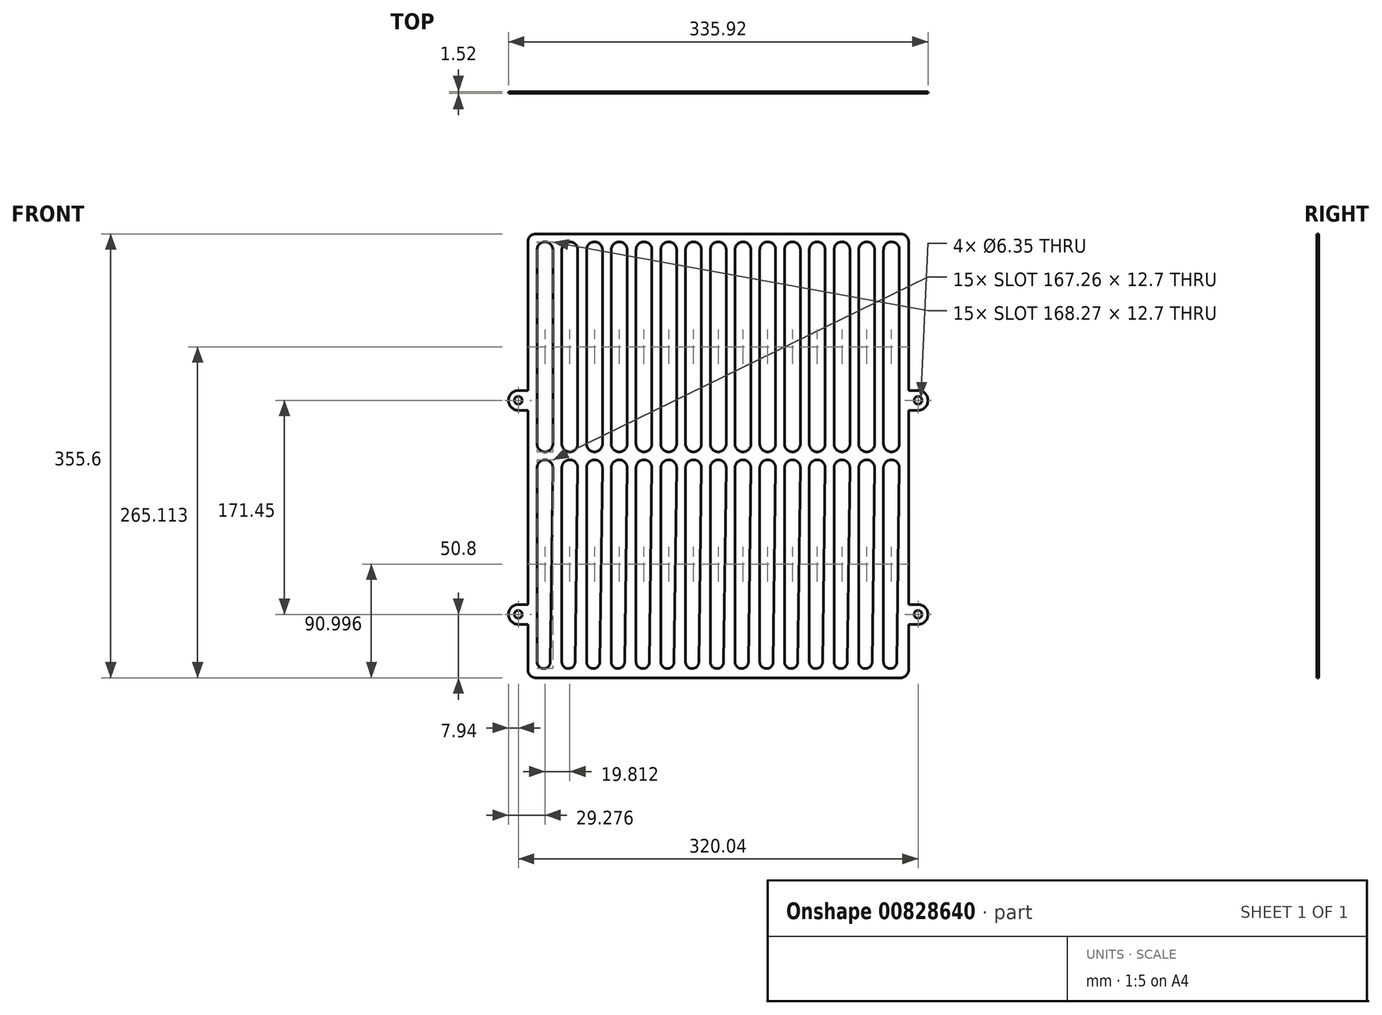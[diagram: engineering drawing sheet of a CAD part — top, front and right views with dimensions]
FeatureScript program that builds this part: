
annotation { "Feature Type Name" : "Feature", "Feature Type Description" : "" }
export const myFeature = defineFeature(function(context is Context, id is Id, definition is map)
    precondition{}
    {
        {
            var Q0;
            Q0=qCreatedBy(makeId("Front.planeOp"),FACE);
            var sketch = newSketch(context, id + "F0", { "sketchPlane" : qUnion([Q0])});
            skLineSegment(sketch, "E0.bottom", {"start": v(-323.85, -177.8) * mm, "end": v(-31.75, -177.8) * mm});
            skLineSegment(sketch, "E0.top", {"start": v(-323.85, 177.8) * mm, "end": v(-31.75, 177.8) * mm});
            skLineSegment(sketch, "E0.left", {"start": v(-330.2, -171.45) * mm, "end": v(-330.2, -134.94) * mm});
            skLineSegment(sketch, "E0.right", {"start": v(-25.4, -171.45) * mm, "end": v(-25.4, -134.94) * mm});
            skPoint(sketch, "E0.middle", {"position": v(-177.8, 0) * mm});
            skArc(sketch, "E1", {"start": v(-337.82, -119.06) * mm, "mid": v(-345.76, -127) * mm, "end": v(-337.82, -134.94) * mm});
            skArc(sketch, "E2", {"start": v(-17.78, -134.94) * mm, "mid": v(-9.84, -127) * mm, "end": v(-17.78, -119.06) * mm});
            skCircle(sketch, "E3", {"center": v(-17.78, -127) * mm, "radius": 3.18 * mm});
            skCircle(sketch, "E4", {"center": v(-337.82, -127) * mm, "radius": 3.18 * mm});
            skLineSegment(sketch, "E5", {"start": v(-17.78, -134.94) * mm, "end": v(-25.4, -134.94) * mm});
            skLineSegment(sketch, "E6", {"start": v(-25.4, -134.94) * mm, "end": v(-25.4, -134.94) * mm});
            skLineSegment(sketch, "E7", {"start": v(-17.78, -119.06) * mm, "end": v(-25.4, -119.06) * mm});
            skLineSegment(sketch, "E8", {"start": v(-337.82, -134.94) * mm, "end": v(-330.2, -134.94) * mm});
            skLineSegment(sketch, "E9", {"start": v(-330.2, -134.94) * mm, "end": v(-330.2, -134.94) * mm});
            skLineSegment(sketch, "E10", {"start": v(-337.82, -119.06) * mm, "end": v(-330.2, -119.06) * mm});
            skLineSegment(sketch, "E11.trimOffspring", {"start": v(-330.2, -119.06) * mm, "end": v(-330.2, 36.51) * mm});
            skLineSegment(sketch, "E12.trimOffspring", {"start": v(-25.4, -119.06) * mm, "end": v(-25.4, 36.51) * mm});
            skPoint(sketch, "E13.end.orphan", {"position": v(-25.4, 29.37) * mm});
            skPoint(sketch, "E13.start.orphan", {"position": v(-330.2, 29.37) * mm});
            skLineSegment(sketch, "E14.MirrorCS", {"start": v(-337.82, 52.39) * mm, "end": v(-330.2, 52.39) * mm});
            skArc(sketch, "E15.MirrorCS", {"start": v(-337.82, 36.51) * mm, "mid": v(-345.76, 44.45) * mm, "end": v(-337.82, 52.39) * mm});
            skCircle(sketch, "E16.MirrorC", {"center": v(-337.82, 44.45) * mm, "radius": 3.18 * mm});
            skLineSegment(sketch, "E17.MirrorCS", {"start": v(-337.82, 36.51) * mm, "end": v(-330.2, 36.51) * mm});
            skLineSegment(sketch, "E18.MirrorCS", {"start": v(-17.78, 52.39) * mm, "end": v(-25.4, 52.39) * mm});
            skArc(sketch, "E19.MirrorCS", {"start": v(-17.78, 52.39) * mm, "mid": v(-9.84, 44.45) * mm, "end": v(-17.78, 36.51) * mm});
            skCircle(sketch, "E20.MirrorC", {"center": v(-17.78, 44.45) * mm, "radius": 3.18 * mm});
            skLineSegment(sketch, "E21.MirrorCS", {"start": v(-17.78, 36.51) * mm, "end": v(-25.4, 36.51) * mm});
            skLineSegment(sketch, "E22.trimOffspring", {"start": v(-25.4, 52.39) * mm, "end": v(-25.4, 171.45) * mm});
            skPoint(sketch, "E23.start.orphan", {"position": v(-330.2, -41.28) * mm});
            skLineSegment(sketch, "E24.trimOffspring", {"start": v(-330.2, 52.39) * mm, "end": v(-330.2, 171.45) * mm});
            skArc(sketch, "E25.0.startCap", {"start": v(-322.83, 165.1) * mm, "mid": v(-316.48, 171.45) * mm, "end": v(-310.13, 165.1) * mm});
            skArc(sketch, "E25.0.endCap", {"start": v(-310.13, 9.52) * mm, "mid": v(-316.48, 3.17) * mm, "end": v(-322.83, 9.52) * mm});
            skLineSegment(sketch, "E25.0.left", {"start": v(-310.13, 165.1) * mm, "end": v(-310.13, 9.52) * mm});
            skLineSegment(sketch, "E25.0.right", {"start": v(-322.83, 165.1) * mm, "end": v(-322.83, 9.52) * mm});
            skArc(sketch, "E25.1.startCap", {"start": v(-322.83, -9.53) * mm, "mid": v(-316.44, -3.18) * mm, "end": v(-310.13, -9.6) * mm});
            skArc(sketch, "E25.1.endCap", {"start": v(-312.17, -165.17) * mm, "mid": v(-317.53, -170.43) * mm, "end": v(-322.83, -165.1) * mm});
            skLineSegment(sketch, "E25.1.left", {"start": v(-310.13, -9.6) * mm, "end": v(-312.17, -165.17) * mm});
            skLineSegment(sketch, "E25.1.right", {"start": v(-322.83, -9.53) * mm, "end": v(-322.83, -165.1) * mm});
            skLineSegment(sketch, "E26.1.0.0", {"start": v(-290.32, 165.1) * mm, "end": v(-290.32, 9.53) * mm});
            skArc(sketch, "E26.1.0.1", {"start": v(-290.32, 9.53) * mm, "mid": v(-296.67, 3.17) * mm, "end": v(-303.02, 9.52) * mm});
            skLineSegment(sketch, "E26.1.0.2", {"start": v(-303.02, 165.1) * mm, "end": v(-303.02, 9.52) * mm});
            skArc(sketch, "E26.1.0.3", {"start": v(-303.02, 165.1) * mm, "mid": v(-296.67, 171.45) * mm, "end": v(-290.32, 165.1) * mm});
            skLineSegment(sketch, "E26.2.0.0", {"start": v(-270.51, 165.1) * mm, "end": v(-270.51, 9.52) * mm});
            skArc(sketch, "E26.2.0.1", {"start": v(-270.51, 9.52) * mm, "mid": v(-276.86, 3.17) * mm, "end": v(-283.21, 9.52) * mm});
            skLineSegment(sketch, "E26.2.0.2", {"start": v(-283.21, 165.1) * mm, "end": v(-283.21, 9.52) * mm});
            skArc(sketch, "E26.2.0.3", {"start": v(-283.21, 165.1) * mm, "mid": v(-276.86, 171.45) * mm, "end": v(-270.51, 165.1) * mm});
            skLineSegment(sketch, "E26.3.0.0", {"start": v(-250.7, 165.1) * mm, "end": v(-250.7, 9.52) * mm});
            skArc(sketch, "E26.3.0.1", {"start": v(-250.7, 9.52) * mm, "mid": v(-257.05, 3.17) * mm, "end": v(-263.4, 9.52) * mm});
            skLineSegment(sketch, "E26.3.0.2", {"start": v(-263.4, 165.1) * mm, "end": v(-263.4, 9.52) * mm});
            skArc(sketch, "E26.3.0.3", {"start": v(-263.4, 165.1) * mm, "mid": v(-257.05, 171.45) * mm, "end": v(-250.7, 165.1) * mm});
            skLineSegment(sketch, "E26.4.0.0", {"start": v(-230.89, 165.1) * mm, "end": v(-230.89, 9.52) * mm});
            skArc(sketch, "E26.4.0.1", {"start": v(-230.89, 9.52) * mm, "mid": v(-237.24, 3.17) * mm, "end": v(-243.59, 9.52) * mm});
            skLineSegment(sketch, "E26.4.0.2", {"start": v(-243.59, 165.1) * mm, "end": v(-243.59, 9.52) * mm});
            skArc(sketch, "E26.4.0.3", {"start": v(-243.59, 165.1) * mm, "mid": v(-237.24, 171.45) * mm, "end": v(-230.89, 165.1) * mm});
            skLineSegment(sketch, "E26.5.0.0", {"start": v(-211.07, 165.1) * mm, "end": v(-211.07, 9.52) * mm});
            skArc(sketch, "E26.5.0.1", {"start": v(-211.07, 9.52) * mm, "mid": v(-217.42, 3.17) * mm, "end": v(-223.77, 9.52) * mm});
            skLineSegment(sketch, "E26.5.0.2", {"start": v(-223.77, 165.1) * mm, "end": v(-223.77, 9.52) * mm});
            skArc(sketch, "E26.5.0.3", {"start": v(-223.77, 165.1) * mm, "mid": v(-217.42, 171.45) * mm, "end": v(-211.07, 165.1) * mm});
            skLineSegment(sketch, "E26.6.0.0", {"start": v(-191.26, 165.1) * mm, "end": v(-191.26, 9.52) * mm});
            skArc(sketch, "E26.6.0.1", {"start": v(-191.26, 9.52) * mm, "mid": v(-197.61, 3.17) * mm, "end": v(-203.96, 9.52) * mm});
            skLineSegment(sketch, "E26.6.0.2", {"start": v(-203.96, 165.1) * mm, "end": v(-203.96, 9.52) * mm});
            skArc(sketch, "E26.6.0.3", {"start": v(-203.96, 165.1) * mm, "mid": v(-197.61, 171.45) * mm, "end": v(-191.26, 165.1) * mm});
            skLineSegment(sketch, "E26.7.0.0", {"start": v(-171.45, 165.1) * mm, "end": v(-171.45, 9.52) * mm});
            skArc(sketch, "E26.7.0.1", {"start": v(-171.45, 9.52) * mm, "mid": v(-177.8, 3.17) * mm, "end": v(-184.15, 9.52) * mm});
            skLineSegment(sketch, "E26.7.0.2", {"start": v(-184.15, 165.1) * mm, "end": v(-184.15, 9.52) * mm});
            skArc(sketch, "E26.7.0.3", {"start": v(-184.15, 165.1) * mm, "mid": v(-177.8, 171.45) * mm, "end": v(-171.45, 165.1) * mm});
            skLineSegment(sketch, "E26.8.0.0", {"start": v(-151.64, 165.1) * mm, "end": v(-151.64, 9.52) * mm});
            skArc(sketch, "E26.8.0.1", {"start": v(-151.64, 9.52) * mm, "mid": v(-157.99, 3.17) * mm, "end": v(-164.34, 9.52) * mm});
            skLineSegment(sketch, "E26.8.0.2", {"start": v(-164.34, 165.1) * mm, "end": v(-164.34, 9.52) * mm});
            skArc(sketch, "E26.8.0.3", {"start": v(-164.34, 165.1) * mm, "mid": v(-157.99, 171.45) * mm, "end": v(-151.64, 165.1) * mm});
            skLineSegment(sketch, "E26.9.0.0", {"start": v(-131.83, 165.1) * mm, "end": v(-131.83, 9.52) * mm});
            skArc(sketch, "E26.9.0.1", {"start": v(-131.83, 9.52) * mm, "mid": v(-138.18, 3.17) * mm, "end": v(-144.53, 9.52) * mm});
            skLineSegment(sketch, "E26.9.0.2", {"start": v(-144.53, 165.1) * mm, "end": v(-144.53, 9.52) * mm});
            skArc(sketch, "E26.9.0.3", {"start": v(-144.53, 165.1) * mm, "mid": v(-138.18, 171.45) * mm, "end": v(-131.83, 165.1) * mm});
            skLineSegment(sketch, "E26.10.0.0", {"start": v(-112.01, 165.1) * mm, "end": v(-112.01, 9.52) * mm});
            skArc(sketch, "E26.10.0.1", {"start": v(-112.01, 9.52) * mm, "mid": v(-118.36, 3.17) * mm, "end": v(-124.71, 9.52) * mm});
            skLineSegment(sketch, "E26.10.0.2", {"start": v(-124.71, 165.1) * mm, "end": v(-124.71, 9.52) * mm});
            skArc(sketch, "E26.10.0.3", {"start": v(-124.71, 165.1) * mm, "mid": v(-118.36, 171.45) * mm, "end": v(-112.01, 165.1) * mm});
            skLineSegment(sketch, "E26.11.0.0", {"start": v(-92.2, 165.1) * mm, "end": v(-92.2, 9.52) * mm});
            skArc(sketch, "E26.11.0.1", {"start": v(-92.2, 9.52) * mm, "mid": v(-98.55, 3.17) * mm, "end": v(-104.9, 9.52) * mm});
            skLineSegment(sketch, "E26.11.0.2", {"start": v(-104.9, 165.1) * mm, "end": v(-104.9, 9.52) * mm});
            skArc(sketch, "E26.11.0.3", {"start": v(-104.9, 165.1) * mm, "mid": v(-98.55, 171.45) * mm, "end": v(-92.2, 165.1) * mm});
            skLineSegment(sketch, "E26.direction1", {"start": v(-310.13, 9.52) * mm, "end": v(-290.32, 9.52) * mm, "construction": true});
            skLineSegment(sketch, "E26.direction2", {"start": v(-310.13, 9.52) * mm, "end": v(-310.13, 34.92) * mm, "construction": true});
            skLineSegment(sketch, "E27.0.12.0", {"start": v(-72.4, 165.1) * mm, "end": v(-72.4, 9.52) * mm});
            skArc(sketch, "E27.3.12.0", {"start": v(-72.4, 9.52) * mm, "mid": v(-78.74, 3.17) * mm, "end": v(-85.1, 9.52) * mm});
            skLineSegment(sketch, "E27.7.12.0", {"start": v(-85.1, 165.1) * mm, "end": v(-85.1, 9.52) * mm});
            skArc(sketch, "E27.10.12.0", {"start": v(-85.1, 165.1) * mm, "mid": v(-78.74, 171.45) * mm, "end": v(-72.4, 165.1) * mm});
            skLineSegment(sketch, "E27.0.13.0", {"start": v(-52.58, 165.1) * mm, "end": v(-52.58, 9.52) * mm});
            skArc(sketch, "E27.3.13.0", {"start": v(-52.58, 9.52) * mm, "mid": v(-58.93, 3.17) * mm, "end": v(-65.28, 9.52) * mm});
            skLineSegment(sketch, "E27.7.13.0", {"start": v(-65.28, 165.1) * mm, "end": v(-65.28, 9.52) * mm});
            skArc(sketch, "E27.10.13.0", {"start": v(-65.28, 165.1) * mm, "mid": v(-58.93, 171.45) * mm, "end": v(-52.58, 165.1) * mm});
            skLineSegment(sketch, "E27.0.14.0", {"start": v(-32.77, 165.1) * mm, "end": v(-32.77, 9.52) * mm});
            skArc(sketch, "E27.3.14.0", {"start": v(-32.77, 9.52) * mm, "mid": v(-39.12, 3.17) * mm, "end": v(-45.47, 9.52) * mm});
            skLineSegment(sketch, "E27.7.14.0", {"start": v(-45.47, 165.1) * mm, "end": v(-45.47, 9.52) * mm});
            skArc(sketch, "E27.10.14.0", {"start": v(-45.47, 165.1) * mm, "mid": v(-39.12, 171.45) * mm, "end": v(-32.77, 165.1) * mm});
            skLineSegment(sketch, "E28.1.0.0", {"start": v(-303.02, -9.53) * mm, "end": v(-303.02, -165.1) * mm});
            skArc(sketch, "E28.1.0.1", {"start": v(-292.35, -165.17) * mm, "mid": v(-297.72, -170.43) * mm, "end": v(-303.02, -165.1) * mm});
            skLineSegment(sketch, "E28.1.0.2", {"start": v(-290.32, -9.6) * mm, "end": v(-292.35, -165.17) * mm});
            skArc(sketch, "E28.1.0.3", {"start": v(-303.02, -9.53) * mm, "mid": v(-296.63, -3.18) * mm, "end": v(-290.32, -9.6) * mm});
            skLineSegment(sketch, "E28.2.0.0", {"start": v(-283.21, -9.53) * mm, "end": v(-283.21, -165.1) * mm});
            skArc(sketch, "E28.2.0.1", {"start": v(-272.54, -165.17) * mm, "mid": v(-277.91, -170.43) * mm, "end": v(-283.21, -165.1) * mm});
            skLineSegment(sketch, "E28.2.0.2", {"start": v(-270.51, -9.6) * mm, "end": v(-272.54, -165.17) * mm});
            skArc(sketch, "E28.2.0.3", {"start": v(-283.21, -9.53) * mm, "mid": v(-276.82, -3.18) * mm, "end": v(-270.51, -9.6) * mm});
            skLineSegment(sketch, "E28.3.0.0", {"start": v(-263.4, -9.53) * mm, "end": v(-263.4, -165.1) * mm});
            skArc(sketch, "E28.3.0.1", {"start": v(-252.73, -165.17) * mm, "mid": v(-258.1, -170.43) * mm, "end": v(-263.4, -165.1) * mm});
            skLineSegment(sketch, "E28.3.0.2", {"start": v(-250.7, -9.6) * mm, "end": v(-252.73, -165.17) * mm});
            skArc(sketch, "E28.3.0.3", {"start": v(-263.4, -9.53) * mm, "mid": v(-257, -3.18) * mm, "end": v(-250.7, -9.6) * mm});
            skLineSegment(sketch, "E28.4.0.0", {"start": v(-243.59, -9.53) * mm, "end": v(-243.59, -165.1) * mm});
            skArc(sketch, "E28.4.0.1", {"start": v(-232.92, -165.17) * mm, "mid": v(-238.29, -170.43) * mm, "end": v(-243.59, -165.1) * mm});
            skLineSegment(sketch, "E28.4.0.2", {"start": v(-230.89, -9.6) * mm, "end": v(-232.92, -165.17) * mm});
            skArc(sketch, "E28.4.0.3", {"start": v(-243.59, -9.53) * mm, "mid": v(-237.2, -3.18) * mm, "end": v(-230.89, -9.6) * mm});
            skLineSegment(sketch, "E28.5.0.0", {"start": v(-223.77, -9.53) * mm, "end": v(-223.77, -165.1) * mm});
            skArc(sketch, "E28.5.0.1", {"start": v(-213.1, -165.17) * mm, "mid": v(-218.47, -170.43) * mm, "end": v(-223.77, -165.1) * mm});
            skLineSegment(sketch, "E28.5.0.2", {"start": v(-211.07, -9.6) * mm, "end": v(-213.1, -165.17) * mm});
            skArc(sketch, "E28.5.0.3", {"start": v(-223.77, -9.53) * mm, "mid": v(-217.38, -3.18) * mm, "end": v(-211.07, -9.6) * mm});
            skLineSegment(sketch, "E28.6.0.0", {"start": v(-203.96, -9.53) * mm, "end": v(-203.96, -165.1) * mm});
            skArc(sketch, "E28.6.0.1", {"start": v(-193.3, -165.17) * mm, "mid": v(-198.66, -170.43) * mm, "end": v(-203.96, -165.1) * mm});
            skLineSegment(sketch, "E28.6.0.2", {"start": v(-191.26, -9.6) * mm, "end": v(-193.3, -165.17) * mm});
            skArc(sketch, "E28.6.0.3", {"start": v(-203.96, -9.53) * mm, "mid": v(-197.57, -3.18) * mm, "end": v(-191.26, -9.6) * mm});
            skLineSegment(sketch, "E28.7.0.0", {"start": v(-184.15, -9.53) * mm, "end": v(-184.15, -165.1) * mm});
            skArc(sketch, "E28.7.0.1", {"start": v(-173.48, -165.17) * mm, "mid": v(-178.85, -170.43) * mm, "end": v(-184.15, -165.1) * mm});
            skLineSegment(sketch, "E28.7.0.2", {"start": v(-171.45, -9.6) * mm, "end": v(-173.48, -165.17) * mm});
            skArc(sketch, "E28.7.0.3", {"start": v(-184.15, -9.53) * mm, "mid": v(-177.76, -3.18) * mm, "end": v(-171.45, -9.6) * mm});
            skLineSegment(sketch, "E28.8.0.0", {"start": v(-164.34, -9.53) * mm, "end": v(-164.34, -165.1) * mm});
            skArc(sketch, "E28.8.0.1", {"start": v(-153.67, -165.17) * mm, "mid": v(-159.04, -170.43) * mm, "end": v(-164.34, -165.1) * mm});
            skLineSegment(sketch, "E28.8.0.2", {"start": v(-151.64, -9.6) * mm, "end": v(-153.67, -165.17) * mm});
            skArc(sketch, "E28.8.0.3", {"start": v(-164.34, -9.53) * mm, "mid": v(-157.95, -3.18) * mm, "end": v(-151.64, -9.6) * mm});
            skLineSegment(sketch, "E28.9.0.0", {"start": v(-144.53, -9.53) * mm, "end": v(-144.53, -165.1) * mm});
            skArc(sketch, "E28.9.0.1", {"start": v(-133.86, -165.17) * mm, "mid": v(-139.23, -170.43) * mm, "end": v(-144.53, -165.1) * mm});
            skLineSegment(sketch, "E28.9.0.2", {"start": v(-131.83, -9.6) * mm, "end": v(-133.86, -165.17) * mm});
            skArc(sketch, "E28.9.0.3", {"start": v(-144.53, -9.53) * mm, "mid": v(-138.13, -3.18) * mm, "end": v(-131.83, -9.6) * mm});
            skLineSegment(sketch, "E28.10.0.0", {"start": v(-124.71, -9.53) * mm, "end": v(-124.71, -165.1) * mm});
            skArc(sketch, "E28.10.0.1", {"start": v(-114.05, -165.17) * mm, "mid": v(-119.41, -170.43) * mm, "end": v(-124.71, -165.1) * mm});
            skLineSegment(sketch, "E28.10.0.2", {"start": v(-112.01, -9.6) * mm, "end": v(-114.05, -165.17) * mm});
            skArc(sketch, "E28.10.0.3", {"start": v(-124.71, -9.53) * mm, "mid": v(-118.32, -3.18) * mm, "end": v(-112.01, -9.6) * mm});
            skLineSegment(sketch, "E28.11.0.0", {"start": v(-104.9, -9.53) * mm, "end": v(-104.9, -165.1) * mm});
            skArc(sketch, "E28.11.0.1", {"start": v(-94.23, -165.17) * mm, "mid": v(-99.6, -170.43) * mm, "end": v(-104.9, -165.1) * mm});
            skLineSegment(sketch, "E28.11.0.2", {"start": v(-92.2, -9.6) * mm, "end": v(-94.23, -165.17) * mm});
            skArc(sketch, "E28.11.0.3", {"start": v(-104.9, -9.53) * mm, "mid": v(-98.51, -3.18) * mm, "end": v(-92.2, -9.6) * mm});
            skLineSegment(sketch, "E28.12.0.0", {"start": v(-85.1, -9.53) * mm, "end": v(-85.1, -165.1) * mm});
            skArc(sketch, "E28.12.0.1", {"start": v(-74.42, -165.17) * mm, "mid": v(-79.8, -170.43) * mm, "end": v(-85.1, -165.1) * mm});
            skLineSegment(sketch, "E28.12.0.2", {"start": v(-72.4, -9.6) * mm, "end": v(-74.42, -165.17) * mm});
            skArc(sketch, "E28.12.0.3", {"start": v(-85.1, -9.53) * mm, "mid": v(-78.7, -3.18) * mm, "end": v(-72.4, -9.6) * mm});
            skLineSegment(sketch, "E28.13.0.0", {"start": v(-65.28, -9.53) * mm, "end": v(-65.28, -165.1) * mm});
            skArc(sketch, "E28.13.0.1", {"start": v(-54.61, -165.17) * mm, "mid": v(-59.98, -170.43) * mm, "end": v(-65.28, -165.1) * mm});
            skLineSegment(sketch, "E28.13.0.2", {"start": v(-52.58, -9.6) * mm, "end": v(-54.61, -165.17) * mm});
            skArc(sketch, "E28.13.0.3", {"start": v(-65.28, -9.53) * mm, "mid": v(-58.89, -3.18) * mm, "end": v(-52.58, -9.6) * mm});
            skLineSegment(sketch, "E28.14.0.0", {"start": v(-45.47, -9.53) * mm, "end": v(-45.47, -165.1) * mm});
            skArc(sketch, "E28.14.0.1", {"start": v(-34.8, -165.17) * mm, "mid": v(-40.17, -170.43) * mm, "end": v(-45.47, -165.1) * mm});
            skLineSegment(sketch, "E28.14.0.2", {"start": v(-32.77, -9.6) * mm, "end": v(-34.8, -165.17) * mm});
            skArc(sketch, "E28.14.0.3", {"start": v(-45.47, -9.53) * mm, "mid": v(-39.07, -3.18) * mm, "end": v(-32.77, -9.6) * mm});
            skLineSegment(sketch, "E28.direction1", {"start": v(-322.83, -165.1) * mm, "end": v(-303.02, -165.1) * mm, "construction": true});
            skPoint(sketch, "E29.visualSharp", {"position": v(-25.4, -177.8) * mm});
            skArc(sketch, "E29.filletArc", {"start": v(-31.75, -177.8) * mm, "mid": v(-27.26, -175.94) * mm, "end": v(-25.4, -171.45) * mm});
            skPoint(sketch, "E30.visualSharp", {"position": v(-25.4, 177.8) * mm});
            skArc(sketch, "E30.filletArc", {"start": v(-25.4, 171.45) * mm, "mid": v(-27.26, 175.94) * mm, "end": v(-31.75, 177.8) * mm});
            skPoint(sketch, "E31.visualSharp", {"position": v(-330.2, 177.8) * mm});
            skArc(sketch, "E31.filletArc", {"start": v(-323.85, 177.8) * mm, "mid": v(-328.34, 175.94) * mm, "end": v(-330.2, 171.45) * mm});
            skPoint(sketch, "E32.visualSharp", {"position": v(-330.2, -177.8) * mm});
            skArc(sketch, "E32.filletArc", {"start": v(-330.2, -171.45) * mm, "mid": v(-328.34, -175.94) * mm, "end": v(-323.85, -177.8) * mm});
            skSolve(sketch);
        }
        {
            var Q0;
            Q0=makeQuery(id+"F0.imprint","IMPRINT",FACE,{"disambiguationData":[TD([[makeQuery(id+"F0.imprint","IMPRINT",EDGE,{"derivedFrom":sQuery(id+"F0.wireOp",EDGE,"E0.bottom")}),1.0]])]});
            extrude(context, id + "F1", {"entities" : qUnion([Q0]), "depth" : 1.52 * mm, "offsetDistance" : 25.4 * mm});
        }
    });
